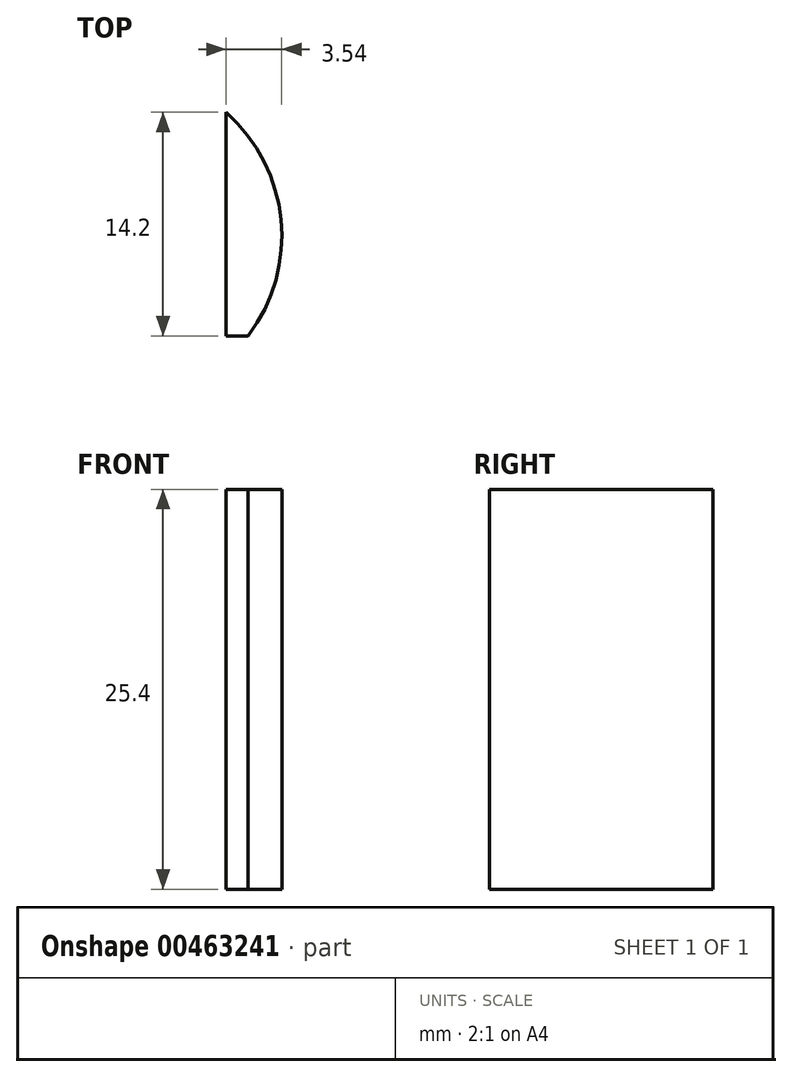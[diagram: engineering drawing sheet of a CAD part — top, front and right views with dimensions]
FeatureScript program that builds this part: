
annotation { "Feature Type Name" : "Feature", "Feature Type Description" : "" }
export const myFeature = defineFeature(function(context is Context, id is Id, definition is map)
    precondition{}
    {
        {
            var Q0;
            Q0=qCreatedBy(makeId("Top.planeOp"),FACE);
            var sketch = newSketch(context, id + "F0", { "sketchPlane" : qUnion([Q0])});
            skLineSegment(sketch, "E0.bottom", {"start": v(-46.12, -43.54) * mm, "end": v(-23.31, -43.54) * mm});
            skLineSegment(sketch, "E0.top", {"start": v(-46.12, -16.4) * mm, "end": v(-23.31, -16.4) * mm});
            skLineSegment(sketch, "E0.left", {"start": v(-46.12, -43.54) * mm, "end": v(-46.12, -16.4) * mm});
            skLineSegment(sketch, "E0.right", {"start": v(-23.31, -43.54) * mm, "end": v(-23.31, -16.4) * mm});
            skSolve(sketch);
        }
        {
            var Q0;
            Q0 = qSketchRegion(id + "F0", true);
            extrude(context, id + "F1", {"entities" : qUnion([Q0]), "oppositeDirection" : true, "depth" : 38.86 * mm});
        }
        {
            var Q0;
            Q0=makeQuery(id+"F1.opExtrude","CAP_FACE",FACE,{"disambiguationData":[OSD([sQuery(id+"F0.wireOp",EDGE,"E0.bottom"),sQuery(id+"F0.wireOp",EDGE,"E0.top"),sQuery(id+"F0.wireOp",EDGE,"E0.left"),sQuery(id+"F0.wireOp",EDGE,"E0.right")])],"isStart":false});
            var sketch = newSketch(context, id + "F2", { "sketchPlane" : qUnion([Q0])});
            skCircle(sketch, "E1", {"center": v(-53.05, 37.2) * mm, "radius": 10.47 * mm});
            skSolve(sketch);
        }
        {
            var Q0;
            Q0 = qSketchRegion(id + "F2", true);
            extrude(context, id + "F3", {"entities" : qUnion([Q0]), "operationType" : NewBodyOperationType.INTERSECT, "oppositeDirection" : true, "depth" : 25.4 * mm});
        }
    });
